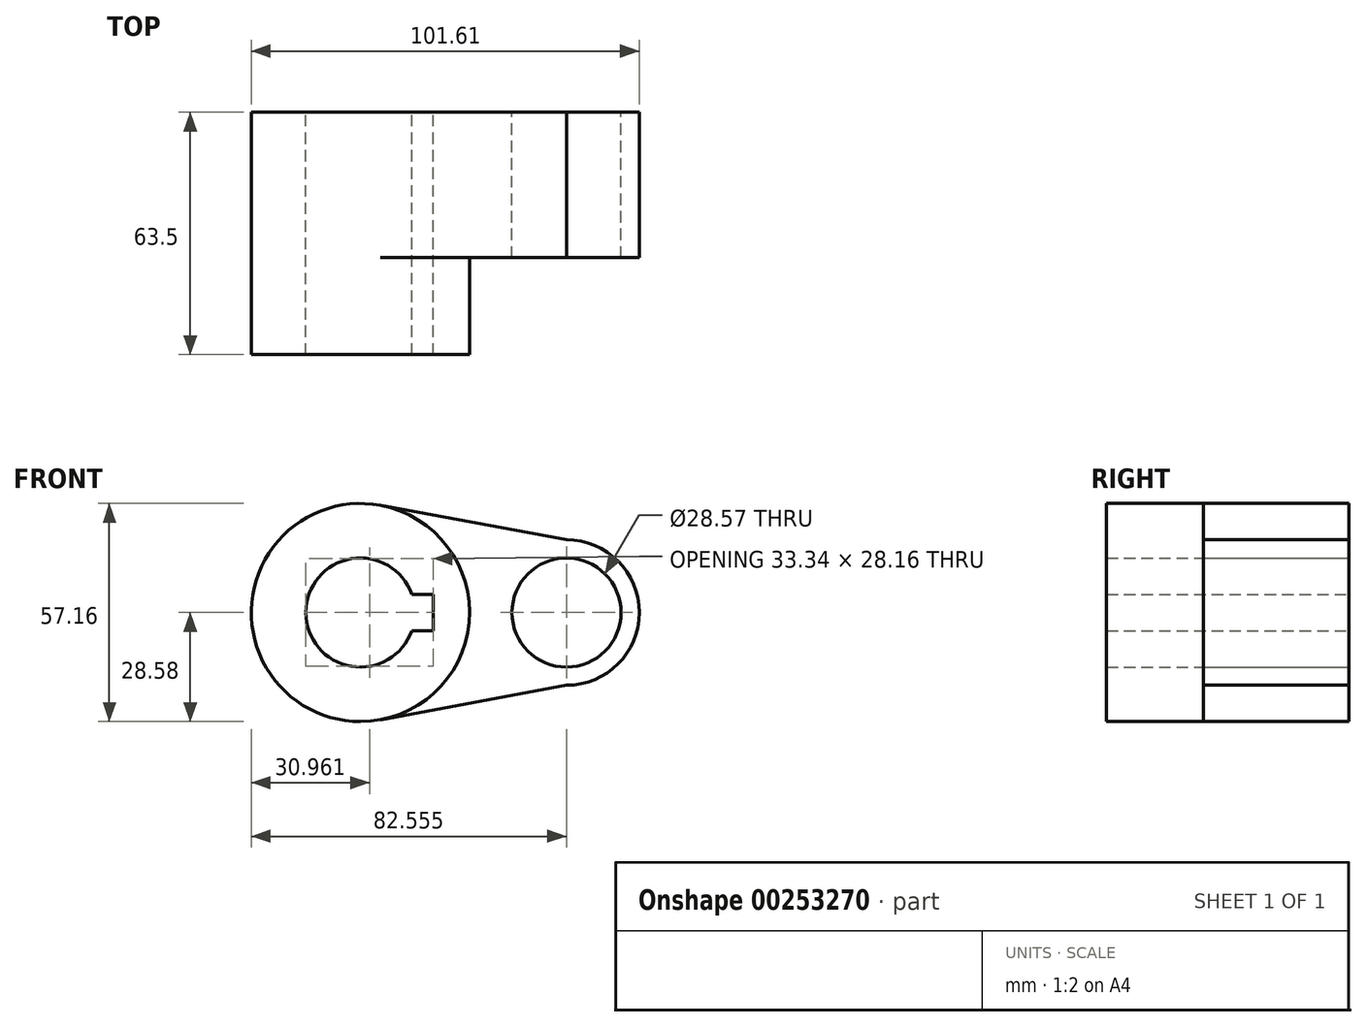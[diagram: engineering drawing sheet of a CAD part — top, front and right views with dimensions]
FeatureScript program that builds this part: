
annotation { "Feature Type Name" : "Feature", "Feature Type Description" : "" }
export const myFeature = defineFeature(function(context is Context, id is Id, definition is map)
    precondition{}
    {
        {
            var Q0;
            Q0=qCreatedBy(makeId("Front.planeOp"),FACE);
            var sketch = newSketch(context, id + "F0", { "sketchPlane" : qUnion([Q0])});
            skCircle(sketch, "E0", {"center": v(0, 0) * mm, "radius": 28.58 * mm});
            skCircle(sketch, "E1", {"center": v(53.98, 0) * mm, "radius": 19.05 * mm});
            skLineSegment(sketch, "E2", {"start": v(5.21, 28.1) * mm, "end": v(53.98, 19.05) * mm});
            skLineSegment(sketch, "E3", {"start": v(5.21, -28.1) * mm, "end": v(53.98, -19.05) * mm});
            skCircle(sketch, "E4", {"center": v(0, 0) * mm, "radius": 14.29 * mm});
            skCircle(sketch, "E5", {"center": v(53.98, 0) * mm, "radius": 14.29 * mm});
            skLineSegment(sketch, "E6.bottom", {"start": v(19.05, 4.76) * mm, "end": v(-19.05, 4.76) * mm});
            skLineSegment(sketch, "E6.top", {"start": v(19.05, -4.76) * mm, "end": v(-19.05, -4.76) * mm});
            skLineSegment(sketch, "E6.left", {"start": v(19.05, 4.76) * mm, "end": v(19.05, -4.76) * mm});
            skLineSegment(sketch, "E6.right", {"start": v(-19.05, 4.76) * mm, "end": v(-19.05, -4.76) * mm});
            skSolve(sketch);
        }
        {
            var Q0;
            {var subQ11=sQuery(id+"F0.wireOp",EDGE,"E6.left");Q0=makeQuery(id+"F0.imprint","IMPRINT",FACE,{"disambiguationData":[TD([[makeQuery(id+"F0.imprint","IMPRINT",EDGE,{"derivedFrom":subQ11}),1.0]])]});}
            var Q1;
            {var subQ0=sQuery(id+"F0.wireOp",EDGE,"E2");Q1=makeQuery(id+"F0.imprint","IMPRINT",FACE,{"disambiguationData":[TD([[makeQuery(id+"F0.imprint","IMPRINT",EDGE,{"derivedFrom":subQ0}),-1.0]])]});}
            var Q2;
            Q2=makeQuery(id+"F0.imprint","IMPRINT",FACE,{"disambiguationData":[TD([[makeQuery(id+"F0.imprint","IMPRINT",EDGE,{"derivedFrom":sQuery(id+"F0.wireOp",EDGE,"E5")}),-1.0]])]});
            var Q3;
            {var subQ5=sQuery(id+"F0.wireOp",EDGE,"E6.right");Q3=makeQuery(id+"F0.imprint","IMPRINT",FACE,{"disambiguationData":[TD([[makeQuery(id+"F0.imprint","IMPRINT",EDGE,{"derivedFrom":subQ5}),1.0]])]});}
            extrude(context, id + "F1", {"entities" : qUnion([Q0, Q1, Q2, Q3]), "depth" : 38.1 * mm});
        }
        {
            var Q0;
            {var subQ11=sQuery(id+"F0.wireOp",EDGE,"E6.left");Q0=makeQuery(id+"F0.imprint","IMPRINT",FACE,{"disambiguationData":[TD([[makeQuery(id+"F0.imprint","IMPRINT",EDGE,{"derivedFrom":subQ11}),1.0]])]});}
            var Q1;
            {var subQ5=sQuery(id+"F0.wireOp",EDGE,"E6.right");Q1=makeQuery(id+"F0.imprint","IMPRINT",FACE,{"disambiguationData":[TD([[makeQuery(id+"F0.imprint","IMPRINT",EDGE,{"derivedFrom":subQ5}),1.0]])]});}
            extrude(context, id + "F2", {"entities" : qUnion([Q0, Q1]), "operationType" : NewBodyOperationType.ADD, "depth" : 63.5 * mm});
        }
    });
